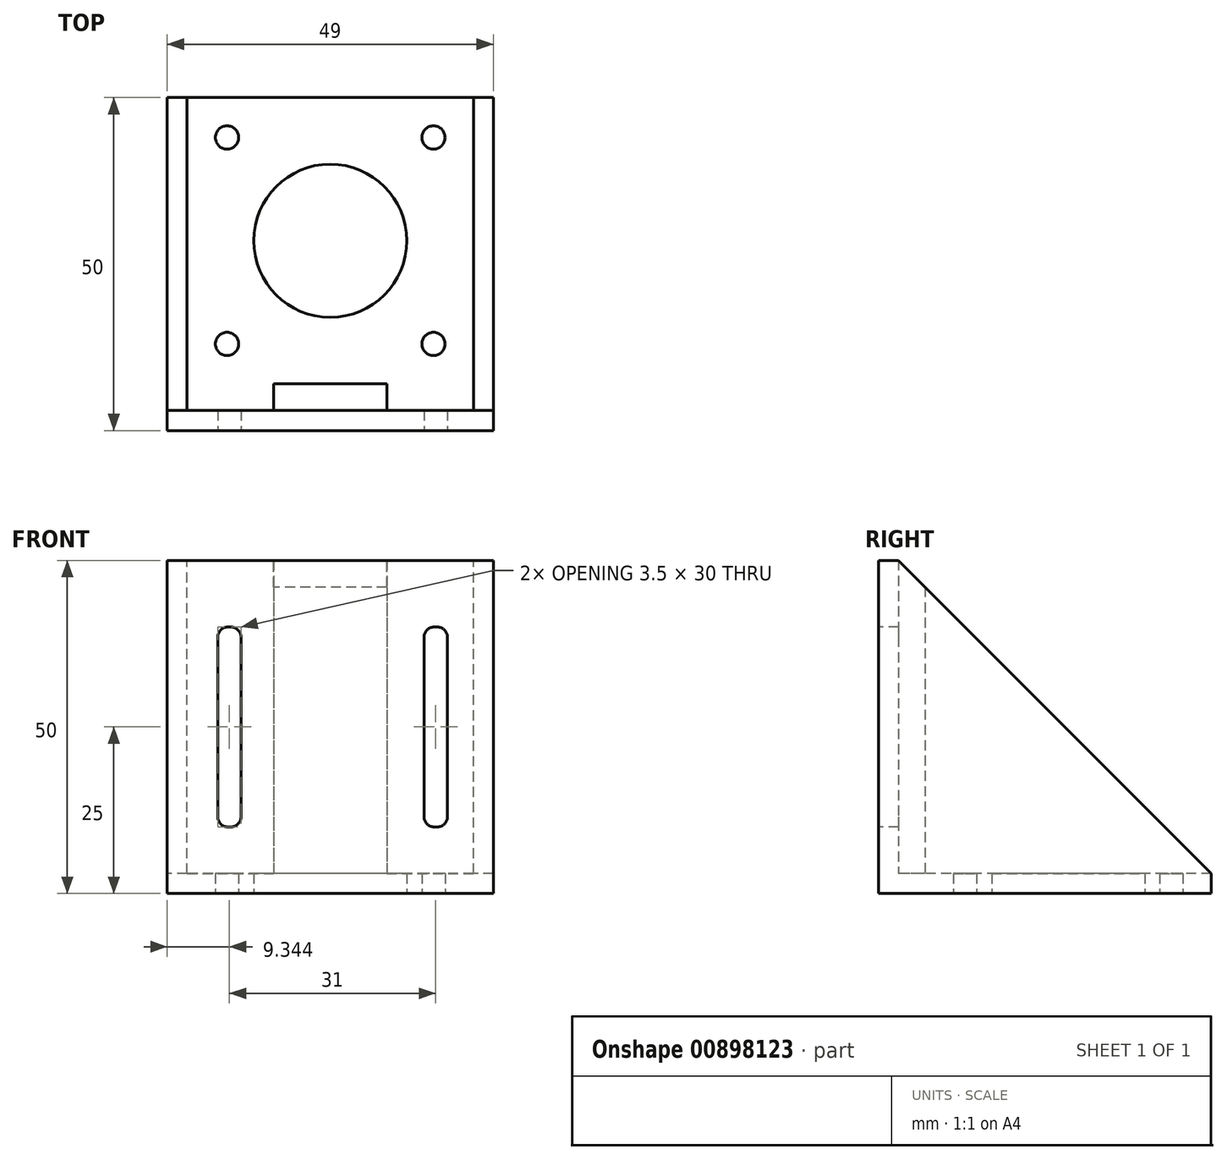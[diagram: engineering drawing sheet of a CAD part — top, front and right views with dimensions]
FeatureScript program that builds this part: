
annotation { "Feature Type Name" : "Feature", "Feature Type Description" : "" }
export const myFeature = defineFeature(function(context is Context, id is Id, definition is map)
    precondition{}
    {
        {
            var Q0;
            Q0=qCreatedBy(makeId("Top.planeOp"),FACE);
            var sketch = newSketch(context, id + "F0", { "sketchPlane" : qUnion([Q0])});
            skLineSegment(sketch, "E0.bottom", {"start": v(21.5, 21.5) * mm, "end": v(-21.5, 21.5) * mm});
            skLineSegment(sketch, "E0.top", {"start": v(21.5, -21.5) * mm, "end": v(-21.5, -21.5) * mm});
            skLineSegment(sketch, "E0.left", {"start": v(21.5, 21.5) * mm, "end": v(21.5, -21.5) * mm});
            skLineSegment(sketch, "E0.right", {"start": v(-21.5, 21.5) * mm, "end": v(-21.5, -21.5) * mm});
            skPoint(sketch, "E0.middle", {"position": v(0, 0) * mm});
            skCircle(sketch, "E1", {"center": v(0, 0) * mm, "radius": 11.5 * mm});
            skCircle(sketch, "E2", {"center": v(15.5, 15.5) * mm, "radius": 1.75 * mm});
            skCircle(sketch, "E3.0.1.0", {"center": v(15.5, -15.5) * mm, "radius": 1.75 * mm});
            skCircle(sketch, "E3.1.0.0", {"center": v(-15.5, 15.5) * mm, "radius": 1.75 * mm});
            skCircle(sketch, "E3.1.1.0", {"center": v(-15.5, -15.5) * mm, "radius": 1.75 * mm});
            skLineSegment(sketch, "E3.direction1", {"start": v(15.5, 15.5) * mm, "end": v(-15.5, 15.5) * mm, "construction": true});
            skLineSegment(sketch, "E3.direction2", {"start": v(15.5, 15.5) * mm, "end": v(15.5, -15.5) * mm, "construction": true});
            skLineSegment(sketch, "E4.top", {"start": v(-24.5, -28.5) * mm, "end": v(24.5, -28.5) * mm});
            skLineSegment(sketch, "E5.top", {"start": v(-24.5, -25.5) * mm, "end": v(24.5, -25.5) * mm});
            skLineSegment(sketch, "E5.left", {"start": v(-24.5, -28.5) * mm, "end": v(-24.5, -25.5) * mm});
            skLineSegment(sketch, "E5.right", {"start": v(24.5, -28.5) * mm, "end": v(24.5, -25.5) * mm});
            skLineSegment(sketch, "E6", {"start": v(-8.5, -21.5) * mm, "end": v(-8.5, -25.5) * mm});
            skLineSegment(sketch, "E7", {"start": v(8.5, -21.5) * mm, "end": v(8.5, -25.5) * mm});
            skLineSegment(sketch, "E8.bottom", {"start": v(-24.5, -25.5) * mm, "end": v(-21.5, -25.5) * mm});
            skLineSegment(sketch, "E8.top", {"start": v(-24.5, 21.5) * mm, "end": v(-21.5, 21.5) * mm});
            skLineSegment(sketch, "E8.left", {"start": v(-24.5, -25.5) * mm, "end": v(-24.5, 21.5) * mm});
            skLineSegment(sketch, "E8.right", {"start": v(-21.5, -25.5) * mm, "end": v(-21.5, 21.5) * mm});
            skLineSegment(sketch, "E9.bottom", {"start": v(21.5, 21.5) * mm, "end": v(24.5, 21.5) * mm});
            skLineSegment(sketch, "E9.top", {"start": v(21.5, -25.5) * mm, "end": v(24.5, -25.5) * mm});
            skLineSegment(sketch, "E9.left", {"start": v(21.5, 21.5) * mm, "end": v(21.5, -25.5) * mm});
            skLineSegment(sketch, "E9.right", {"start": v(24.5, 21.5) * mm, "end": v(24.5, -25.5) * mm});
            skSolve(sketch);
        }
        {
            var Q0;
            Q0=makeQuery(id+"F0.imprint","IMPRINT",FACE,{"disambiguationData":[TD([[makeQuery(id+"F0.imprint","IMPRINT",EDGE,{"derivedFrom":sQuery(id+"F0.wireOp",EDGE,"E0.right")}),-1.0]])]});
            var Q1;
            Q1=makeQuery(id+"F0.imprint","IMPRINT",FACE,{"disambiguationData":[TD([[makeQuery(id+"F0.imprint","IMPRINT",EDGE,{"derivedFrom":sQuery(id+"F0.wireOp",EDGE,"E4.top")}),1.0]])]});
            var Q2;
            Q2=makeQuery(id+"F0.imprint","IMPRINT",FACE,{"disambiguationData":[TD([[makeQuery(id+"F0.imprint","IMPRINT",EDGE,{"derivedFrom":sQuery(id+"F0.wireOp",EDGE,"E0.left")}),1.0]])]});
            var Q3;
            {var subQ2=sQuery(id+"F0.wireOp",EDGE,"E6");Q3=makeQuery(id+"F0.imprint","IMPRINT",FACE,{"disambiguationData":[TD([[makeQuery(id+"F0.imprint","IMPRINT",EDGE,{"derivedFrom":subQ2}),1.0]])]});}
            extrude(context, id + "F1", {"entities" : qUnion([Q0, Q1, Q2, Q3]), "depth" : 50 * mm, "offsetDistance" : 25 * mm});
        }
        {
            var Q0;
            Q0=makeQuery(id+"F0.imprint","IMPRINT",FACE,{"disambiguationData":[TD([[makeQuery(id+"F0.imprint","IMPRINT",EDGE,{"derivedFrom":sQuery(id+"F0.wireOp",EDGE,"E0.bottom")}),1.0]])]});
            var Q1;
            {var subQ0=sQuery(id+"F0.wireOp",EDGE,"E7");Q1=makeQuery(id+"F0.imprint","IMPRINT",FACE,{"disambiguationData":[TD([[makeQuery(id+"F0.imprint","IMPRINT",EDGE,{"derivedFrom":subQ0}),1.0]])]});}
            var Q2;
            {var subQ2=sQuery(id+"F0.wireOp",EDGE,"E6");Q2=makeQuery(id+"F0.imprint","IMPRINT",FACE,{"disambiguationData":[TD([[makeQuery(id+"F0.imprint","IMPRINT",EDGE,{"derivedFrom":subQ2}),-1.0]])]});}
            extrude(context, id + "F2", {"entities" : qUnion([Q0, Q1, Q2]), "operationType" : NewBodyOperationType.ADD, "depth" : 3 * mm, "offsetDistance" : 25 * mm});
        }
        {
            var Q0;
            Q0=makeQuery(id+"F1.opExtrude","SWEPT_FACE",FACE,{"disambiguationData":[OSD([sQuery(id+"F0.wireOp",EDGE,"E0.left"),sQuery(id+"F0.wireOp",EDGE,"E9.left")])]});
            var sketch = newSketch(context, id + "F3", { "sketchPlane" : qUnion([Q0])});
            skLineSegment(sketch, "E10", {"start": v(25.5, 50) * mm, "end": v(-21.5, 3) * mm});
            skLineSegment(sketch, "E11", {"start": v(-21.5, 3) * mm, "end": v(-21.5, 50) * mm});
            skLineSegment(sketch, "E12", {"start": v(-21.5, 50) * mm, "end": v(25.5, 50) * mm});
            skSolve(sketch);
        }
        {
            var Q0;
            Q0=makeQuery(id+"F3.imprint","IMPRINT",FACE,{"disambiguationData":[TD([[makeQuery(id+"F3.imprint","IMPRINT",EDGE,{"derivedFrom":sQuery(id+"F3.wireOp",EDGE,"E10")}),-1.0]])]});
            extrude(context, id + "F4", {"entities" : qUnion([Q0]), "operationType" : NewBodyOperationType.REMOVE, "oppositeDirection" : true, "depth" : 5 * mm, "offsetDistance" : 25 * mm, "hasSecondDirection" : true, "secondDirectionOppositeDirection" : false, "secondDirectionDepth" : 50 * mm});
        }
        {
            var Q0;
            Q0=makeQuery(id+"F1.opExtrude","SWEPT_FACE",FACE,{"disambiguationData":[OSD([sQuery(id+"F0.wireOp",EDGE,"E4.top")])]});
            var sketch = newSketch(context, id + "F5", { "sketchPlane" : qUnion([Q0])});
            skLineSegment(sketch, "E13.bottom", {"start": v(16.1, 40) * mm, "end": v(15.6, 40) * mm});
            skLineSegment(sketch, "E13.top", {"start": v(16.1, 10) * mm, "end": v(15.6, 10) * mm});
            skLineSegment(sketch, "E13.left", {"start": v(17.6, 38.5) * mm, "end": v(17.6, 11.5) * mm});
            skLineSegment(sketch, "E13.right", {"start": v(14.1, 38.5) * mm, "end": v(14.1, 11.5) * mm});
            skPoint(sketch, "E13.middle", {"position": v(15.84, 25) * mm});
            skPoint(sketch, "E14.visualSharp", {"position": v(17.6, 40) * mm});
            skArc(sketch, "E14.filletArc", {"start": v(17.6, 38.5) * mm, "mid": v(17.16, 39.56) * mm, "end": v(16.1, 40) * mm});
            skPoint(sketch, "E15.visualSharp", {"position": v(14.1, 40) * mm});
            skArc(sketch, "E15.filletArc", {"start": v(15.6, 40) * mm, "mid": v(14.53, 39.56) * mm, "end": v(14.1, 38.5) * mm});
            skPoint(sketch, "E16.visualSharp", {"position": v(14.1, 10) * mm});
            skArc(sketch, "E16.filletArc", {"start": v(14.1, 11.5) * mm, "mid": v(14.53, 10.44) * mm, "end": v(15.6, 10) * mm});
            skPoint(sketch, "E17.visualSharp", {"position": v(17.6, 10) * mm});
            skArc(sketch, "E17.filletArc", {"start": v(16.1, 10) * mm, "mid": v(17.16, 10.44) * mm, "end": v(17.6, 11.5) * mm});
            skLineSegment(sketch, "E18.1.0.0", {"start": v(-13.4, 38.5) * mm, "end": v(-13.4, 11.5) * mm});
            skPoint(sketch, "E18.1.0.1", {"position": v(-13.4, 40) * mm});
            skLineSegment(sketch, "E18.1.0.2", {"start": v(-16.9, 38.5) * mm, "end": v(-16.9, 11.5) * mm});
            skPoint(sketch, "E18.1.0.3", {"position": v(-15.16, 25) * mm});
            skPoint(sketch, "E18.1.0.4", {"position": v(-13.4, 10) * mm});
            skPoint(sketch, "E18.1.0.5", {"position": v(-16.9, 40) * mm});
            skPoint(sketch, "E18.1.0.6", {"position": v(-16.9, 10) * mm});
            skArc(sketch, "E18.1.0.7", {"start": v(-13.4, 38.5) * mm, "mid": v(-13.84, 39.56) * mm, "end": v(-14.9, 40) * mm});
            skArc(sketch, "E18.1.0.8", {"start": v(-16.9, 11.5) * mm, "mid": v(-16.47, 10.44) * mm, "end": v(-15.4, 10) * mm});
            skArc(sketch, "E18.1.0.9", {"start": v(-15.4, 40) * mm, "mid": v(-16.47, 39.56) * mm, "end": v(-16.9, 38.5) * mm});
            skArc(sketch, "E18.1.0.10", {"start": v(-14.9, 10) * mm, "mid": v(-13.84, 10.44) * mm, "end": v(-13.4, 11.5) * mm});
            skLineSegment(sketch, "E18.1.0.11", {"start": v(-14.9, 40) * mm, "end": v(-15.4, 40) * mm});
            skLineSegment(sketch, "E18.1.0.12", {"start": v(-14.9, 10) * mm, "end": v(-15.4, 10) * mm});
            skLineSegment(sketch, "E18.direction1", {"start": v(14.1, 10) * mm, "end": v(-16.9, 10) * mm, "construction": true});
            skSolve(sketch);
        }
        {
            var Q0;
            Q0=makeQuery(id+"F5.imprint","IMPRINT",FACE,{"disambiguationData":[TD([[makeQuery(id+"F5.imprint","IMPRINT",EDGE,{"derivedFrom":sQuery(id+"F5.wireOp",EDGE,"E13.bottom")}),1.0]])]});
            var Q1;
            Q1=makeQuery(id+"F5.imprint","IMPRINT",FACE,{"disambiguationData":[TD([[makeQuery(id+"F5.imprint","IMPRINT",EDGE,{"derivedFrom":sQuery(id+"F5.wireOp",EDGE,"E18.1.0.0")}),-1.0]])]});
            extrude(context, id + "F6", {"entities" : qUnion([Q0, Q1]), "operationType" : NewBodyOperationType.REMOVE, "oppositeDirection" : true, "depth" : 3 * mm, "offsetDistance" : 25 * mm});
        }
        {
            var Q0;
            Q0=makeQuery(id+"F1.opExtrude","SWEPT_BODY",BODY,{"disambiguationData":[OSD([sQuery(id+"F0.wireOp",EDGE,"E0.top"),sQuery(id+"F0.wireOp",EDGE,"E0.left"),sQuery(id+"F0.wireOp",EDGE,"E0.right"),sQuery(id+"F0.wireOp",EDGE,"E4.top"),sQuery(id+"F0.wireOp",EDGE,"E5.top"),sQuery(id+"F0.wireOp",EDGE,"E5.left"),sQuery(id+"F0.wireOp",EDGE,"E5.right"),sQuery(id+"F0.wireOp",EDGE,"E6"),sQuery(id+"F0.wireOp",EDGE,"E7"),sQuery(id+"F0.wireOp",EDGE,"E8.top"),sQuery(id+"F0.wireOp",EDGE,"E8.left"),sQuery(id+"F0.wireOp",EDGE,"E8.right"),sQuery(id+"F0.wireOp",EDGE,"E9.bottom"),sQuery(id+"F0.wireOp",EDGE,"E9.left"),sQuery(id+"F0.wireOp",EDGE,"E9.right")])]});
            transform(context, id + "F7", {"entities" : qUnion([Q0]), "transformType" : TransformType.TRANSLATION_3D, "dx" : 0 * mm, "dy" : 0 * mm, "dz" : 0 * mm, "makeCopy" : true});
        }
        {
            var Q0;
            Q0=makeQuery(id+"F7.opPattern","COPY",BODY,{"derivedFrom":makeQuery(id+"F1.opExtrude","SWEPT_BODY",BODY,{"disambiguationData":[OSD([sQuery(id+"F0.wireOp",EDGE,"E0.top"),sQuery(id+"F0.wireOp",EDGE,"E0.left"),sQuery(id+"F0.wireOp",EDGE,"E0.right"),sQuery(id+"F0.wireOp",EDGE,"E4.top"),sQuery(id+"F0.wireOp",EDGE,"E5.top"),sQuery(id+"F0.wireOp",EDGE,"E5.left"),sQuery(id+"F0.wireOp",EDGE,"E5.right"),sQuery(id+"F0.wireOp",EDGE,"E6"),sQuery(id+"F0.wireOp",EDGE,"E7"),sQuery(id+"F0.wireOp",EDGE,"E8.top"),sQuery(id+"F0.wireOp",EDGE,"E8.left"),sQuery(id+"F0.wireOp",EDGE,"E8.right"),sQuery(id+"F0.wireOp",EDGE,"E9.bottom"),sQuery(id+"F0.wireOp",EDGE,"E9.left"),sQuery(id+"F0.wireOp",EDGE,"E9.right")])]}),"instanceName":"1"});
            deleteBodies(context, id + "F8", {"entities" : qUnion([Q0])});
        }
        {
            var Q0;
            Q0=makeQuery(id+"F1.opExtrude","SWEPT_BODY",BODY,{"disambiguationData":[OSD([sQuery(id+"F0.wireOp",EDGE,"E0.top"),sQuery(id+"F0.wireOp",EDGE,"E0.left"),sQuery(id+"F0.wireOp",EDGE,"E0.right"),sQuery(id+"F0.wireOp",EDGE,"E4.top"),sQuery(id+"F0.wireOp",EDGE,"E5.top"),sQuery(id+"F0.wireOp",EDGE,"E5.left"),sQuery(id+"F0.wireOp",EDGE,"E5.right"),sQuery(id+"F0.wireOp",EDGE,"E6"),sQuery(id+"F0.wireOp",EDGE,"E7"),sQuery(id+"F0.wireOp",EDGE,"E8.top"),sQuery(id+"F0.wireOp",EDGE,"E8.left"),sQuery(id+"F0.wireOp",EDGE,"E8.right"),sQuery(id+"F0.wireOp",EDGE,"E9.bottom"),sQuery(id+"F0.wireOp",EDGE,"E9.left"),sQuery(id+"F0.wireOp",EDGE,"E9.right")])]});
            transform(context, id + "F9", {"entities" : qUnion([Q0]), "transformType" : TransformType.TRANSLATION_3D, "dx" : 0 * mm, "dy" : 0 * mm, "dz" : 0 * mm, "makeCopy" : true});
        }
        {
            var Q0;
            Q0=makeQuery(id+"F9.opPattern","COPY",BODY,{"derivedFrom":makeQuery(id+"F1.opExtrude","SWEPT_BODY",BODY,{"disambiguationData":[OSD([sQuery(id+"F0.wireOp",EDGE,"E0.top"),sQuery(id+"F0.wireOp",EDGE,"E0.left"),sQuery(id+"F0.wireOp",EDGE,"E0.right"),sQuery(id+"F0.wireOp",EDGE,"E4.top"),sQuery(id+"F0.wireOp",EDGE,"E5.top"),sQuery(id+"F0.wireOp",EDGE,"E5.left"),sQuery(id+"F0.wireOp",EDGE,"E5.right"),sQuery(id+"F0.wireOp",EDGE,"E6"),sQuery(id+"F0.wireOp",EDGE,"E7"),sQuery(id+"F0.wireOp",EDGE,"E8.top"),sQuery(id+"F0.wireOp",EDGE,"E8.left"),sQuery(id+"F0.wireOp",EDGE,"E8.right"),sQuery(id+"F0.wireOp",EDGE,"E9.bottom"),sQuery(id+"F0.wireOp",EDGE,"E9.left"),sQuery(id+"F0.wireOp",EDGE,"E9.right")])]}),"instanceName":"1"});
            deleteBodies(context, id + "F10", {"entities" : qUnion([Q0])});
        }
    });
